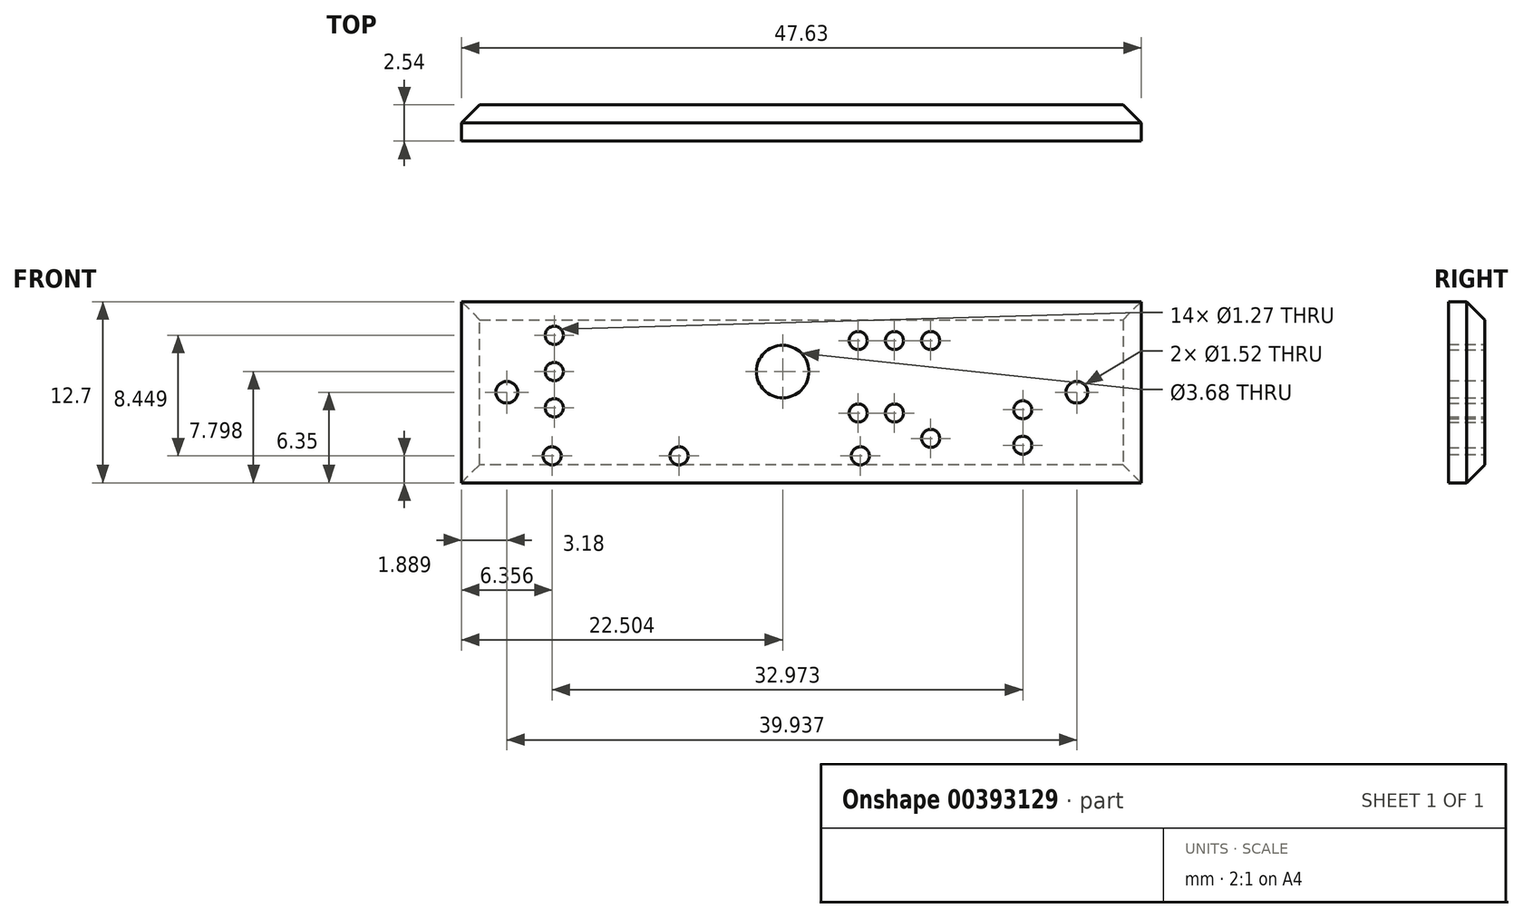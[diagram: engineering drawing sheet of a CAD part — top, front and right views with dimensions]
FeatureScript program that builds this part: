
annotation { "Feature Type Name" : "Feature", "Feature Type Description" : "" }
export const myFeature = defineFeature(function(context is Context, id is Id, definition is map)
    precondition{}
    {
        {
            var Q0;
            Q0=qCreatedBy(makeId("Front.planeOp"),FACE);
            var sketch = newSketch(context, id + "F0", { "sketchPlane" : qUnion([Q0])});
            skLineSegment(sketch, "E0", {"start": v(0, 12.7) * mm, "end": v(44.45, 12.7) * mm});
            skLineSegment(sketch, "E1", {"start": v(44.45, 12.7) * mm, "end": v(44.45, 0) * mm});
            skLineSegment(sketch, "E2", {"start": v(44.45, 0) * mm, "end": v(0, 0) * mm});
            skCircle(sketch, "E3", {"center": v(3.32, 10.34) * mm, "radius": 0.64 * mm});
            skLineSegment(sketch, "E4", {"start": v(3.32, 10.34) * mm, "end": v(3.32, 7.8) * mm});
            skLineSegment(sketch, "E5", {"start": v(3.32, 7.8) * mm, "end": v(3.32, 5.26) * mm});
            skCircle(sketch, "E6", {"center": v(3.32, 7.8) * mm, "radius": 0.64 * mm});
            skCircle(sketch, "E7", {"center": v(3.32, 5.26) * mm, "radius": 0.64 * mm});
            skLineSegment(sketch, "E8", {"start": v(3.32, 7.8) * mm, "end": v(19.32, 7.8) * mm});
            skCircle(sketch, "E9", {"center": v(19.32, 7.8) * mm, "radius": 1.84 * mm});
            skLineSegment(sketch, "E10", {"start": v(3.18, 1.89) * mm, "end": v(12.07, 1.89) * mm});
            skLineSegment(sketch, "E11", {"start": v(12.07, 1.89) * mm, "end": v(24.77, 1.89) * mm});
            skCircle(sketch, "E12", {"center": v(3.18, 1.89) * mm, "radius": 0.64 * mm});
            skCircle(sketch, "E13", {"center": v(12.07, 1.89) * mm, "radius": 0.64 * mm});
            skCircle(sketch, "E14", {"center": v(24.77, 1.89) * mm, "radius": 0.64 * mm});
            skLineSegment(sketch, "E15", {"start": v(24.62, 9.97) * mm, "end": v(24.62, 4.89) * mm});
            skLineSegment(sketch, "E16", {"start": v(24.62, 4.89) * mm, "end": v(27.16, 4.89) * mm});
            skLineSegment(sketch, "E17", {"start": v(27.16, 4.89) * mm, "end": v(27.16, 9.97) * mm});
            skLineSegment(sketch, "E18", {"start": v(27.16, 9.97) * mm, "end": v(29.7, 9.97) * mm});
            skLineSegment(sketch, "E19", {"start": v(29.7, 9.97) * mm, "end": v(29.7, 3.11) * mm});
            skCircle(sketch, "E20", {"center": v(29.7, 3.11) * mm, "radius": 0.64 * mm});
            skCircle(sketch, "E21", {"center": v(29.7, 9.97) * mm, "radius": 0.64 * mm});
            skCircle(sketch, "E22", {"center": v(27.16, 9.97) * mm, "radius": 0.64 * mm});
            skCircle(sketch, "E23", {"center": v(24.62, 9.97) * mm, "radius": 0.64 * mm});
            skCircle(sketch, "E24", {"center": v(24.62, 4.89) * mm, "radius": 0.64 * mm});
            skCircle(sketch, "E25", {"center": v(27.16, 4.89) * mm, "radius": 0.64 * mm});
            skCircle(sketch, "E26", {"center": v(39.94, 6.35) * mm, "radius": 0.76 * mm});
            skPoint(sketch, "E26.centerSnap0", {"position": v(0, 6.35) * mm});
            skCircle(sketch, "E27", {"center": v(0, 6.35) * mm, "radius": 0.76 * mm});
            skLineSegment(sketch, "E28", {"start": v(0, 12.7) * mm, "end": v(-3.18, 12.7) * mm});
            skLineSegment(sketch, "E29", {"start": v(-3.18, 12.7) * mm, "end": v(-3.18, 0) * mm});
            skLineSegment(sketch, "E30", {"start": v(-3.18, 0) * mm, "end": v(0, 0) * mm});
            skLineSegment(sketch, "E31", {"start": v(36.15, 2.63) * mm, "end": v(36.15, 5.12) * mm});
            skCircle(sketch, "E32", {"center": v(36.15, 2.63) * mm, "radius": 0.64 * mm});
            skCircle(sketch, "E33", {"center": v(36.15, 5.12) * mm, "radius": 0.64 * mm});
            skSolve(sketch);
        }
        {
            var Q0;
            Q0=makeQuery(id+"F0.imprint","IMPRINT",FACE,{"disambiguationData":[TD([[makeQuery(id+"F0.imprint","IMPRINT",EDGE,{"derivedFrom":sQuery(id+"F0.wireOp",EDGE,"E0")}),-1.0]])]});
            extrude(context, id + "F1", {"entities" : qUnion([Q0]), "depth" : 2.54 * mm});
        }
        {
            var Q0;
            Q0=makeQuery(id+"F1.opExtrude","CAP_EDGE",EDGE,{"disambiguationData":[OSD([sQuery(id+"F0.wireOp",EDGE,"E1")])],"isStart":true});
            var Q1;
            Q1=makeQuery(id+"F1.opExtrude","CAP_EDGE",EDGE,{"disambiguationData":[OSD([sQuery(id+"F0.wireOp",EDGE,"E0"),sQuery(id+"F0.wireOp",EDGE,"E28")])],"isStart":true});
            var Q2;
            Q2=makeQuery(id+"F1.opExtrude","CAP_EDGE",EDGE,{"disambiguationData":[OSD([sQuery(id+"F0.wireOp",EDGE,"E2"),sQuery(id+"F0.wireOp",EDGE,"E30")])],"isStart":true});
            var Q3;
            Q3=makeQuery(id+"F1.opExtrude","CAP_EDGE",EDGE,{"disambiguationData":[OSD([sQuery(id+"F0.wireOp",EDGE,"E29")])],"isStart":true});
            chamfer(context, id + "F2", {"entities" : qUnion([Q0, Q1, Q2, Q3]), "width" : 1.27 * mm, "tangentPropagation" : true});
        }
    });
